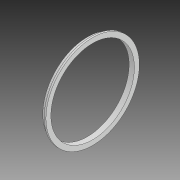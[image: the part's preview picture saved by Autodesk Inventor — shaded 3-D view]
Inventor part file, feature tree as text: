
AUTODESK INVENTOR PART (.ipt)
format: ipt  version: 2020 (Build 240168000, 168)  size: 96,768 bytes
history: native  units: mm
features: revolve x1, sketch x1
ambient origin geometry x8: Origin, YZ Plane, XZ Plane, XY Plane, X Axis, Y Axis, Z Axis, Center Point
bodies: Solid1 (feature_tree)
feature tree (2):
  revolve  "Revolution1"  Angle=90.0deg
  sketch  "Sketch1"  dims[d0=63.4mm d1=4.0mm d2=2.5mm d3=3.0mm d4=5.0mm d8=90.0deg]
